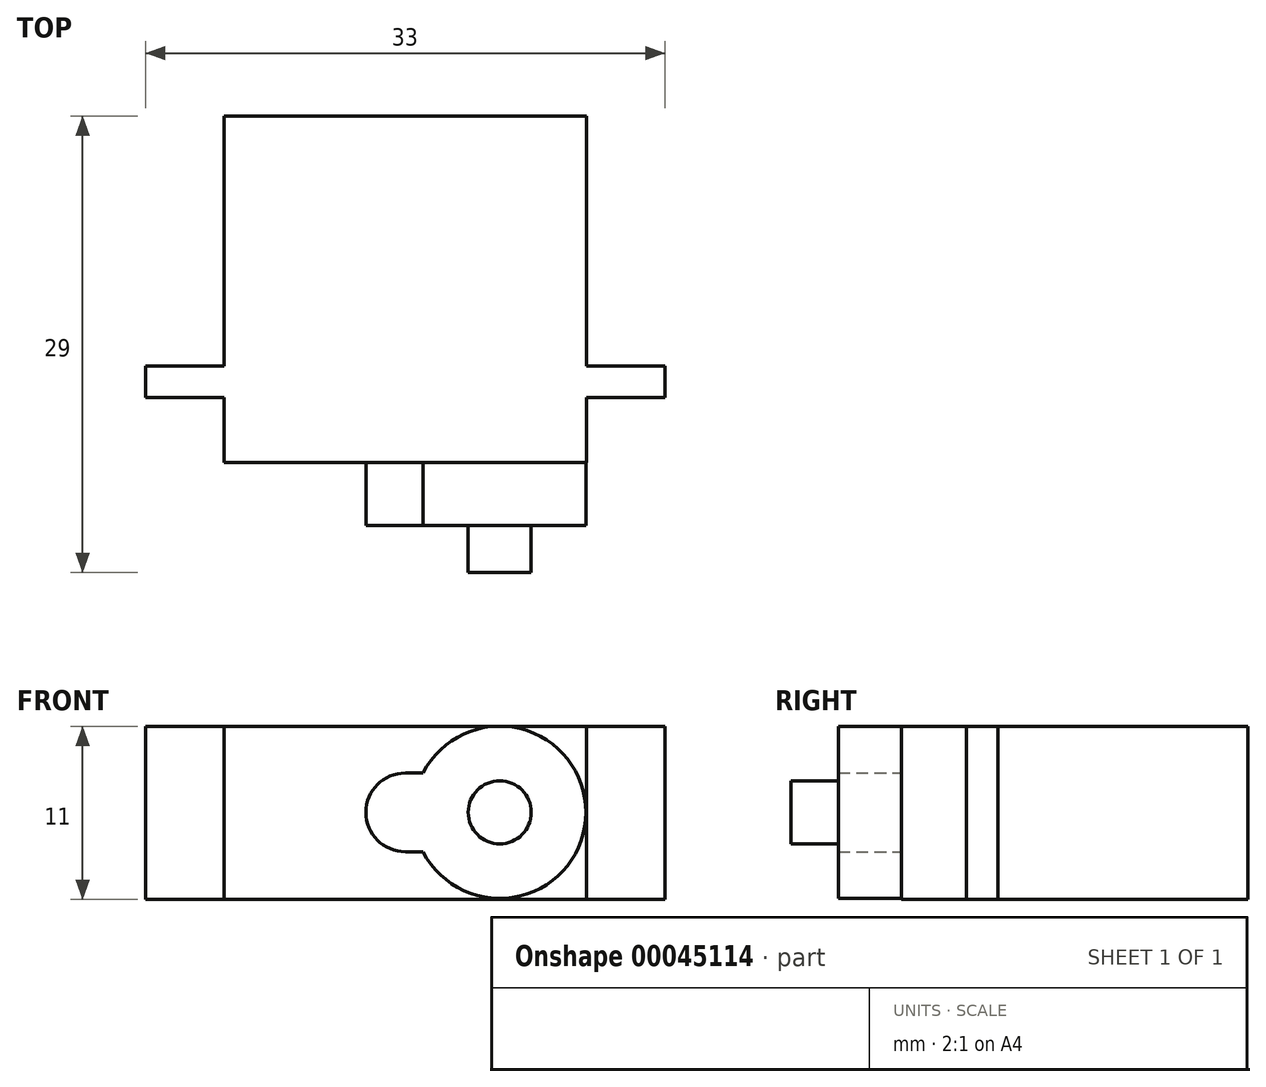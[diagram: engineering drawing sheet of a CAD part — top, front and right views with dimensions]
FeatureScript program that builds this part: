
annotation { "Feature Type Name" : "Feature", "Feature Type Description" : "" }
export const myFeature = defineFeature(function(context is Context, id is Id, definition is map)
    precondition{}
    {
        {
            var Q0;
            Q0=qCreatedBy(makeId("Top.planeOp"),FACE);
            var sketch = newSketch(context, id + "F0", { "sketchPlane" : qUnion([Q0])});
            skLineSegment(sketch, "E0.rect.bottom", {"start": v(11.5, 11) * mm, "end": v(-11.5, 11) * mm});
            skLineSegment(sketch, "E0.rect.top", {"start": v(11.5, -11) * mm, "end": v(-11.5, -11) * mm});
            skLineSegment(sketch, "E0.rect.left", {"start": v(11.5, 11) * mm, "end": v(11.5, -11) * mm});
            skLineSegment(sketch, "E0.rect.right", {"start": v(-11.5, 11) * mm, "end": v(-11.5, -11) * mm});
            skPoint(sketch, "E0.rect.middle", {"position": v(0, 0) * mm});
            skLineSegment(sketch, "E1", {"start": v(-11.5, -4.86) * mm, "end": v(-16.5, -4.86) * mm});
            skLineSegment(sketch, "E2", {"start": v(-16.5, -4.86) * mm, "end": v(-16.5, -6.86) * mm});
            skLineSegment(sketch, "E3", {"start": v(-16.5, -6.86) * mm, "end": v(-11.5, -6.86) * mm});
            skLineSegment(sketch, "E4", {"start": v(-11.5, -6.86) * mm, "end": v(-11.5, -4.86) * mm});
            skLineSegment(sketch, "E5", {"start": v(-11.5, -4.86) * mm, "end": v(11.5, -4.86) * mm});
            skLineSegment(sketch, "E6", {"start": v(11.5, -4.86) * mm, "end": v(16.5, -4.86) * mm});
            skLineSegment(sketch, "E7", {"start": v(16.5, -4.86) * mm, "end": v(16.5, -6.86) * mm});
            skLineSegment(sketch, "E8", {"start": v(16.5, -6.86) * mm, "end": v(11.5, -6.86) * mm});
            skSolve(sketch);
        }
        {
            var Q0;
            Q0 = qSketchRegion(id + "F0", true);
            extrude(context, id + "F1", {"entities" : qUnion([Q0]), "depth" : 11 * mm});
        }
        {
            var Q0;
            Q0=makeQuery(id+"F1.opExtrude","SWEPT_FACE",FACE,{"disambiguationData":[OSD([sQuery(id+"F0.wireOp",EDGE,"E0.rect.top")])]});
            var sketch = newSketch(context, id + "F2", { "sketchPlane" : qUnion([Q0])});
            skLineSegment(sketch, "E9", {"start": v(0, 0) * mm, "end": v(11.47, 0) * mm});
            skLineSegment(sketch, "E10", {"start": v(11.47, 0) * mm, "end": v(11.5, 5.5) * mm});
            skLineSegment(sketch, "E11", {"start": v(11.5, 5.5) * mm, "end": v(6, 5.53) * mm});
            skCircle(sketch, "E12", {"center": v(6, 5.53) * mm, "radius": 5.47 * mm});
            skLineSegment(sketch, "E13", {"start": v(0, 8.03) * mm, "end": v(1.13, 8.03) * mm});
            skLineSegment(sketch, "E14", {"start": v(0, 3.03) * mm, "end": v(1.13, 3.03) * mm});
            skArc(sketch, "E15", {"start": v(0, 8.03) * mm, "mid": v(-2.5, 5.53) * mm, "end": v(0, 3.03) * mm});
            skSolve(sketch);
        }
        {
            var Q0;
            Q0 = qSketchRegion(id + "F2", true);
            extrude(context, id + "F3", {"entities" : qUnion([Q0]), "operationType" : NewBodyOperationType.ADD, "depth" : 4 * mm});
        }
        {
            var Q0;
            Q0=makeQuery(id+"F3.opExtrude","CAP_FACE",FACE,{"disambiguationData":[OSD([sQuery(id+"F2.wireOp",EDGE,"E12"),sQuery(id+"F2.wireOp",EDGE,"E13"),sQuery(id+"F2.wireOp",EDGE,"E14"),sQuery(id+"F2.wireOp",EDGE,"E15")])],"isStart":false});
            var sketch = newSketch(context, id + "F4", { "sketchPlane" : qUnion([Q0])});
            skCircle(sketch, "E16", {"center": v(6, 5.53) * mm, "radius": 2 * mm});
            skSolve(sketch);
        }
        {
            var Q0;
            Q0 = qSketchRegion(id + "F4", true);
            extrude(context, id + "F5", {"entities" : qUnion([Q0]), "operationType" : NewBodyOperationType.ADD, "depth" : 3 * mm});
        }
    });
